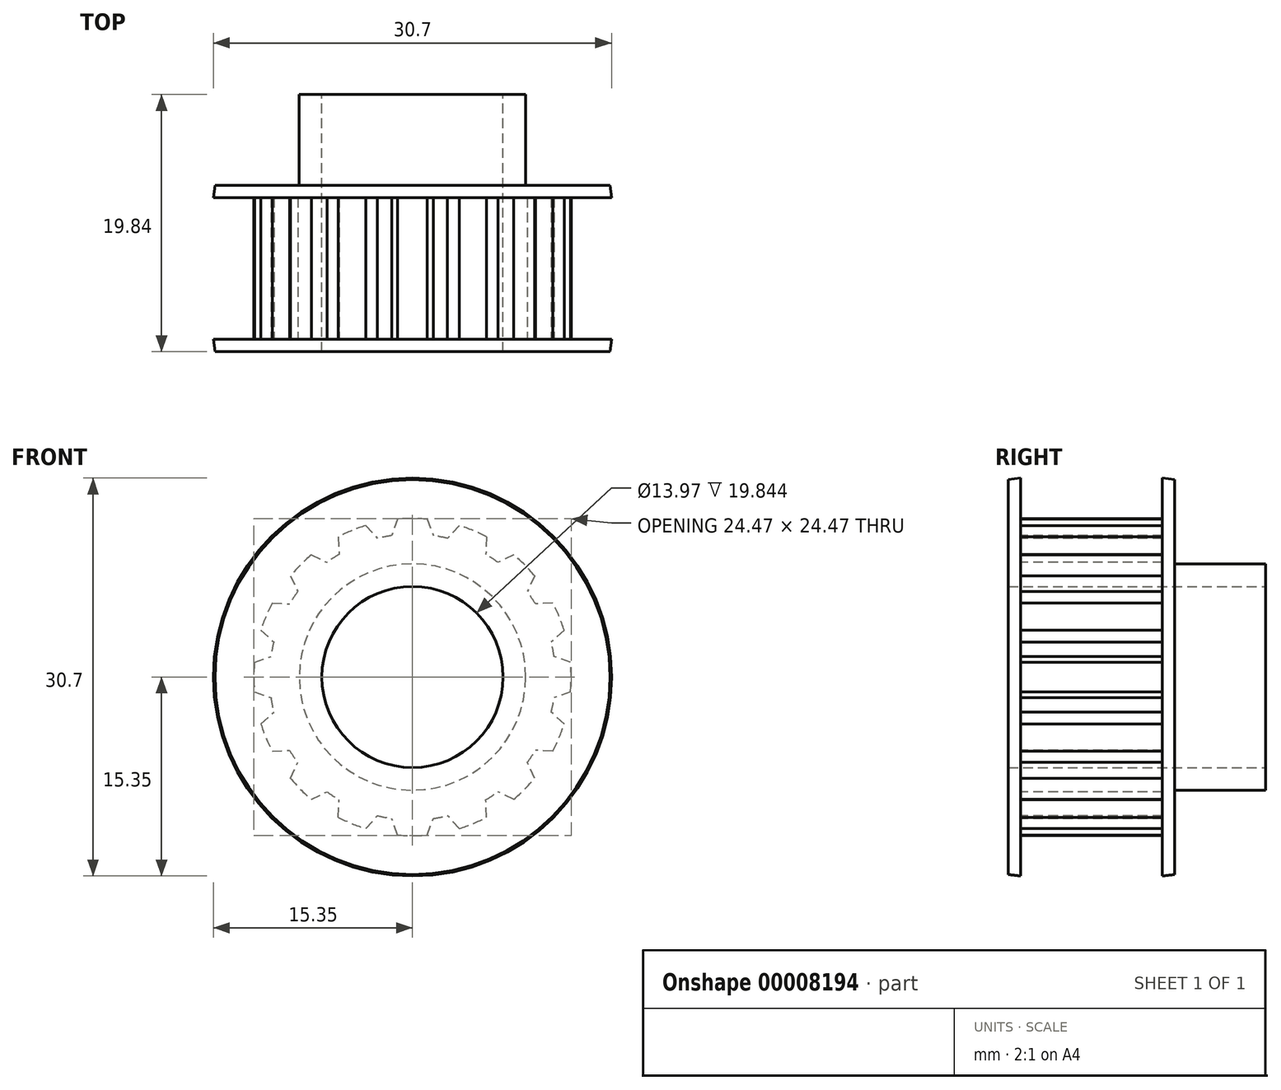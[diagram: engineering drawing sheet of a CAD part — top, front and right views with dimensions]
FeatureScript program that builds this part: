
annotation { "Feature Type Name" : "Feature", "Feature Type Description" : "" }
export const myFeature = defineFeature(function(context is Context, id is Id, definition is map)
    precondition{}
    {
        {
            var Q0;
            Q0=qCreatedBy(makeId("Front.planeOp"),FACE);
            var sketch = newSketch(context, id + "F0", { "sketchPlane" : qUnion([Q0])});
            skArc(sketch, "E0", {"start": v(1.14, 12.18) * mm, "mid": v(0, 12.23) * mm, "end": v(-1.14, 12.18) * mm});
            skArc(sketch, "E1", {"start": v(2.72, 10.7) * mm, "mid": v(2.16, 10.82) * mm, "end": v(1.6, 10.91) * mm});
            skLineSegment(sketch, "E2", {"start": v(0, 0) * mm, "end": v(0, 19.84) * mm, "construction": true});
            skLineSegment(sketch, "E3", {"start": v(-1.14, 12.18) * mm, "end": v(-1.6, 10.91) * mm});
            skLineSegment(sketch, "E4", {"start": v(1.14, 12.18) * mm, "end": v(1.6, 10.91) * mm});
            skLineSegment(sketch, "E5.1.0", {"start": v(-5.71, 10.82) * mm, "end": v(-5.65, 9.47) * mm});
            skArc(sketch, "E5.1.1", {"start": v(-3.6, 11.69) * mm, "mid": v(-4.68, 11.3) * mm, "end": v(-5.71, 10.82) * mm});
            skLineSegment(sketch, "E5.1.2", {"start": v(-3.6, 11.69) * mm, "end": v(-2.7, 10.7) * mm});
            skArc(sketch, "E5.1.3", {"start": v(-1.58, 10.92) * mm, "mid": v(-2.14, 10.82) * mm, "end": v(-2.7, 10.7) * mm});
            skLineSegment(sketch, "E5.2.0", {"start": v(-9.42, 7.8) * mm, "end": v(-8.85, 6.59) * mm});
            skArc(sketch, "E5.2.1", {"start": v(-7.8, 9.42) * mm, "mid": v(-8.65, 8.65) * mm, "end": v(-9.42, 7.8) * mm});
            skLineSegment(sketch, "E5.2.2", {"start": v(-7.8, 9.42) * mm, "end": v(-6.59, 8.85) * mm});
            skArc(sketch, "E5.2.3", {"start": v(-5.64, 9.48) * mm, "mid": v(-6.12, 9.18) * mm, "end": v(-6.59, 8.85) * mm});
            skLineSegment(sketch, "E5.3.0", {"start": v(-11.69, 3.6) * mm, "end": v(-10.7, 2.7) * mm});
            skArc(sketch, "E5.3.1", {"start": v(-10.82, 5.71) * mm, "mid": v(-11.3, 4.68) * mm, "end": v(-11.69, 3.6) * mm});
            skLineSegment(sketch, "E5.3.2", {"start": v(-10.82, 5.71) * mm, "end": v(-9.47, 5.65) * mm});
            skArc(sketch, "E5.3.3", {"start": v(-8.84, 6.6) * mm, "mid": v(-9.17, 6.14) * mm, "end": v(-9.47, 5.65) * mm});
            skLineSegment(sketch, "E5.4.0", {"start": v(-12.18, -1.14) * mm, "end": v(-10.91, -1.6) * mm});
            skArc(sketch, "E5.4.1", {"start": v(-12.18, 1.14) * mm, "mid": v(-12.23, 0) * mm, "end": v(-12.18, -1.14) * mm});
            skLineSegment(sketch, "E5.4.2", {"start": v(-12.18, 1.14) * mm, "end": v(-10.91, 1.6) * mm});
            skArc(sketch, "E5.4.3", {"start": v(-10.7, 2.72) * mm, "mid": v(-10.82, 2.16) * mm, "end": v(-10.91, 1.6) * mm});
            skLineSegment(sketch, "E5.5.0", {"start": v(-10.82, -5.71) * mm, "end": v(-9.47, -5.65) * mm});
            skArc(sketch, "E5.5.1", {"start": v(-11.69, -3.6) * mm, "mid": v(-11.3, -4.68) * mm, "end": v(-10.82, -5.71) * mm});
            skLineSegment(sketch, "E5.5.2", {"start": v(-11.69, -3.6) * mm, "end": v(-10.7, -2.7) * mm});
            skArc(sketch, "E5.5.3", {"start": v(-10.92, -1.58) * mm, "mid": v(-10.82, -2.14) * mm, "end": v(-10.7, -2.7) * mm});
            skLineSegment(sketch, "E5.6.0", {"start": v(-7.8, -9.42) * mm, "end": v(-6.59, -8.85) * mm});
            skArc(sketch, "E5.6.1", {"start": v(-9.42, -7.8) * mm, "mid": v(-8.65, -8.65) * mm, "end": v(-7.8, -9.42) * mm});
            skLineSegment(sketch, "E5.6.2", {"start": v(-9.42, -7.8) * mm, "end": v(-8.85, -6.59) * mm});
            skArc(sketch, "E5.6.3", {"start": v(-9.48, -5.64) * mm, "mid": v(-9.18, -6.12) * mm, "end": v(-8.85, -6.59) * mm});
            skLineSegment(sketch, "E5.7.0", {"start": v(-3.6, -11.69) * mm, "end": v(-2.7, -10.7) * mm});
            skArc(sketch, "E5.7.1", {"start": v(-5.71, -10.82) * mm, "mid": v(-4.68, -11.3) * mm, "end": v(-3.6, -11.69) * mm});
            skLineSegment(sketch, "E5.7.2", {"start": v(-5.71, -10.82) * mm, "end": v(-5.65, -9.47) * mm});
            skArc(sketch, "E5.7.3", {"start": v(-6.6, -8.84) * mm, "mid": v(-6.14, -9.17) * mm, "end": v(-5.65, -9.47) * mm});
            skLineSegment(sketch, "E5.8.0", {"start": v(1.14, -12.18) * mm, "end": v(1.6, -10.91) * mm});
            skArc(sketch, "E5.8.1", {"start": v(-1.14, -12.18) * mm, "mid": v(0, -12.23) * mm, "end": v(1.14, -12.18) * mm});
            skLineSegment(sketch, "E5.8.2", {"start": v(-1.14, -12.18) * mm, "end": v(-1.6, -10.91) * mm});
            skArc(sketch, "E5.8.3", {"start": v(-2.72, -10.7) * mm, "mid": v(-2.16, -10.82) * mm, "end": v(-1.6, -10.91) * mm});
            skLineSegment(sketch, "E5.9.0", {"start": v(5.71, -10.82) * mm, "end": v(5.65, -9.47) * mm});
            skArc(sketch, "E5.9.1", {"start": v(3.6, -11.69) * mm, "mid": v(4.68, -11.3) * mm, "end": v(5.71, -10.82) * mm});
            skLineSegment(sketch, "E5.9.2", {"start": v(3.6, -11.69) * mm, "end": v(2.7, -10.7) * mm});
            skArc(sketch, "E5.9.3", {"start": v(1.58, -10.92) * mm, "mid": v(2.14, -10.82) * mm, "end": v(2.7, -10.7) * mm});
            skLineSegment(sketch, "E5.10.0", {"start": v(9.42, -7.8) * mm, "end": v(8.85, -6.59) * mm});
            skArc(sketch, "E5.10.1", {"start": v(7.8, -9.42) * mm, "mid": v(8.65, -8.65) * mm, "end": v(9.42, -7.8) * mm});
            skLineSegment(sketch, "E5.10.2", {"start": v(7.8, -9.42) * mm, "end": v(6.59, -8.85) * mm});
            skArc(sketch, "E5.10.3", {"start": v(5.64, -9.48) * mm, "mid": v(6.12, -9.18) * mm, "end": v(6.59, -8.85) * mm});
            skLineSegment(sketch, "E5.11.0", {"start": v(11.69, -3.6) * mm, "end": v(10.7, -2.7) * mm});
            skArc(sketch, "E5.11.1", {"start": v(10.82, -5.71) * mm, "mid": v(11.3, -4.68) * mm, "end": v(11.69, -3.6) * mm});
            skLineSegment(sketch, "E5.11.2", {"start": v(10.82, -5.71) * mm, "end": v(9.47, -5.65) * mm});
            skArc(sketch, "E5.11.3", {"start": v(8.84, -6.6) * mm, "mid": v(9.17, -6.14) * mm, "end": v(9.47, -5.65) * mm});
            skLineSegment(sketch, "E5.12.0", {"start": v(12.18, 1.14) * mm, "end": v(10.91, 1.6) * mm});
            skArc(sketch, "E5.12.1", {"start": v(12.18, -1.14) * mm, "mid": v(12.23, 0) * mm, "end": v(12.18, 1.14) * mm});
            skLineSegment(sketch, "E5.12.2", {"start": v(12.18, -1.14) * mm, "end": v(10.91, -1.6) * mm});
            skArc(sketch, "E5.12.3", {"start": v(10.7, -2.72) * mm, "mid": v(10.82, -2.16) * mm, "end": v(10.91, -1.6) * mm});
            skLineSegment(sketch, "E5.13.0", {"start": v(10.82, 5.71) * mm, "end": v(9.47, 5.65) * mm});
            skArc(sketch, "E5.13.1", {"start": v(11.69, 3.6) * mm, "mid": v(11.3, 4.68) * mm, "end": v(10.82, 5.71) * mm});
            skLineSegment(sketch, "E5.13.2", {"start": v(11.69, 3.6) * mm, "end": v(10.7, 2.7) * mm});
            skArc(sketch, "E5.13.3", {"start": v(10.92, 1.58) * mm, "mid": v(10.82, 2.14) * mm, "end": v(10.7, 2.7) * mm});
            skLineSegment(sketch, "E5.14.0", {"start": v(7.8, 9.42) * mm, "end": v(6.59, 8.85) * mm});
            skArc(sketch, "E5.14.1", {"start": v(9.42, 7.8) * mm, "mid": v(8.65, 8.65) * mm, "end": v(7.8, 9.42) * mm});
            skLineSegment(sketch, "E5.14.2", {"start": v(9.42, 7.8) * mm, "end": v(8.85, 6.59) * mm});
            skArc(sketch, "E5.14.3", {"start": v(9.48, 5.64) * mm, "mid": v(9.18, 6.12) * mm, "end": v(8.85, 6.59) * mm});
            skLineSegment(sketch, "E5.15.0", {"start": v(3.6, 11.69) * mm, "end": v(2.7, 10.7) * mm});
            skArc(sketch, "E5.15.1", {"start": v(5.71, 10.82) * mm, "mid": v(4.68, 11.3) * mm, "end": v(3.6, 11.69) * mm});
            skLineSegment(sketch, "E5.15.2", {"start": v(5.71, 10.82) * mm, "end": v(5.65, 9.47) * mm});
            skArc(sketch, "E5.15.3", {"start": v(6.6, 8.84) * mm, "mid": v(6.14, 9.17) * mm, "end": v(5.65, 9.47) * mm});
            skSolve(sketch);
        }
        {
            var Q0;
            Q0=makeQuery(id+"F0.imprint","IMPRINT",FACE,{"disambiguationData":[TD([[makeQuery(id+"F0.imprint","IMPRINT",EDGE,{"derivedFrom":sQuery(id+"F0.wireOp",EDGE,"E0")}),1.0]])]});
            extrude(context, id + "F1", {"entities" : qUnion([Q0]), "oppositeDirection" : true, "depth" : 10.92 * mm});
        }
        {
            var Q0;
            Q0=makeQuery(id+"F1.opExtrude","CAP_FACE",FACE,{"disambiguationData":[OSD([sQuery(id+"F0.wireOp",EDGE,"E0"),sQuery(id+"F0.wireOp",EDGE,"E1"),sQuery(id+"F0.wireOp",EDGE,"E3"),sQuery(id+"F0.wireOp",EDGE,"E4"),sQuery(id+"F0.wireOp",EDGE,"E5.1.0"),sQuery(id+"F0.wireOp",EDGE,"E5.1.1"),sQuery(id+"F0.wireOp",EDGE,"E5.1.2"),sQuery(id+"F0.wireOp",EDGE,"E5.1.3"),sQuery(id+"F0.wireOp",EDGE,"E5.2.0"),sQuery(id+"F0.wireOp",EDGE,"E5.2.1"),sQuery(id+"F0.wireOp",EDGE,"E5.2.2"),sQuery(id+"F0.wireOp",EDGE,"E5.2.3"),sQuery(id+"F0.wireOp",EDGE,"E5.3.0"),sQuery(id+"F0.wireOp",EDGE,"E5.3.1"),sQuery(id+"F0.wireOp",EDGE,"E5.3.2"),sQuery(id+"F0.wireOp",EDGE,"E5.3.3"),sQuery(id+"F0.wireOp",EDGE,"E5.4.0"),sQuery(id+"F0.wireOp",EDGE,"E5.4.1"),sQuery(id+"F0.wireOp",EDGE,"E5.4.2"),sQuery(id+"F0.wireOp",EDGE,"E5.4.3"),sQuery(id+"F0.wireOp",EDGE,"E5.5.0"),sQuery(id+"F0.wireOp",EDGE,"E5.5.1"),sQuery(id+"F0.wireOp",EDGE,"E5.5.2"),sQuery(id+"F0.wireOp",EDGE,"E5.5.3"),sQuery(id+"F0.wireOp",EDGE,"E5.6.0"),sQuery(id+"F0.wireOp",EDGE,"E5.6.1"),sQuery(id+"F0.wireOp",EDGE,"E5.6.2"),sQuery(id+"F0.wireOp",EDGE,"E5.6.3"),sQuery(id+"F0.wireOp",EDGE,"E5.7.0"),sQuery(id+"F0.wireOp",EDGE,"E5.7.1"),sQuery(id+"F0.wireOp",EDGE,"E5.7.2"),sQuery(id+"F0.wireOp",EDGE,"E5.7.3"),sQuery(id+"F0.wireOp",EDGE,"E5.8.0"),sQuery(id+"F0.wireOp",EDGE,"E5.8.1"),sQuery(id+"F0.wireOp",EDGE,"E5.8.2"),sQuery(id+"F0.wireOp",EDGE,"E5.8.3"),sQuery(id+"F0.wireOp",EDGE,"E5.9.0"),sQuery(id+"F0.wireOp",EDGE,"E5.9.1"),sQuery(id+"F0.wireOp",EDGE,"E5.9.2"),sQuery(id+"F0.wireOp",EDGE,"E5.9.3"),sQuery(id+"F0.wireOp",EDGE,"E5.10.0"),sQuery(id+"F0.wireOp",EDGE,"E5.10.1"),sQuery(id+"F0.wireOp",EDGE,"E5.10.2"),sQuery(id+"F0.wireOp",EDGE,"E5.10.3"),sQuery(id+"F0.wireOp",EDGE,"E5.11.0"),sQuery(id+"F0.wireOp",EDGE,"E5.11.1"),sQuery(id+"F0.wireOp",EDGE,"E5.11.2"),sQuery(id+"F0.wireOp",EDGE,"E5.11.3"),sQuery(id+"F0.wireOp",EDGE,"E5.12.0"),sQuery(id+"F0.wireOp",EDGE,"E5.12.1"),sQuery(id+"F0.wireOp",EDGE,"E5.12.2"),sQuery(id+"F0.wireOp",EDGE,"E5.12.3"),sQuery(id+"F0.wireOp",EDGE,"E5.13.0"),sQuery(id+"F0.wireOp",EDGE,"E5.13.1"),sQuery(id+"F0.wireOp",EDGE,"E5.13.2"),sQuery(id+"F0.wireOp",EDGE,"E5.13.3"),sQuery(id+"F0.wireOp",EDGE,"E5.14.0"),sQuery(id+"F0.wireOp",EDGE,"E5.14.1"),sQuery(id+"F0.wireOp",EDGE,"E5.14.2"),sQuery(id+"F0.wireOp",EDGE,"E5.14.3"),sQuery(id+"F0.wireOp",EDGE,"E5.15.0"),sQuery(id+"F0.wireOp",EDGE,"E5.15.1"),sQuery(id+"F0.wireOp",EDGE,"E5.15.2"),sQuery(id+"F0.wireOp",EDGE,"E5.15.3")])],"isStart":true});
            var sketch = newSketch(context, id + "F2", { "sketchPlane" : qUnion([Q0])});
            skCircle(sketch, "E6", {"center": v(0, 0) * mm, "radius": 12.3 * mm});
            skSolve(sketch);
        }
        {
            var Q0;
            Q0 = qSketchRegion(id + "F2", true);
            extrude(context, id + "F3", {"entities" : qUnion([Q0]), "operationType" : NewBodyOperationType.ADD, "depth" : 0.96 * mm});
        }
        {
            var Q0;
            Q0=makeQuery(id+"F1.opExtrude","CAP_FACE",FACE,{"disambiguationData":[OSD([sQuery(id+"F0.wireOp",EDGE,"E0"),sQuery(id+"F0.wireOp",EDGE,"E1"),sQuery(id+"F0.wireOp",EDGE,"E3"),sQuery(id+"F0.wireOp",EDGE,"E4"),sQuery(id+"F0.wireOp",EDGE,"E5.1.0"),sQuery(id+"F0.wireOp",EDGE,"E5.1.1"),sQuery(id+"F0.wireOp",EDGE,"E5.1.2"),sQuery(id+"F0.wireOp",EDGE,"E5.1.3"),sQuery(id+"F0.wireOp",EDGE,"E5.2.0"),sQuery(id+"F0.wireOp",EDGE,"E5.2.1"),sQuery(id+"F0.wireOp",EDGE,"E5.2.2"),sQuery(id+"F0.wireOp",EDGE,"E5.2.3"),sQuery(id+"F0.wireOp",EDGE,"E5.3.0"),sQuery(id+"F0.wireOp",EDGE,"E5.3.1"),sQuery(id+"F0.wireOp",EDGE,"E5.3.2"),sQuery(id+"F0.wireOp",EDGE,"E5.3.3"),sQuery(id+"F0.wireOp",EDGE,"E5.4.0"),sQuery(id+"F0.wireOp",EDGE,"E5.4.1"),sQuery(id+"F0.wireOp",EDGE,"E5.4.2"),sQuery(id+"F0.wireOp",EDGE,"E5.4.3"),sQuery(id+"F0.wireOp",EDGE,"E5.5.0"),sQuery(id+"F0.wireOp",EDGE,"E5.5.1"),sQuery(id+"F0.wireOp",EDGE,"E5.5.2"),sQuery(id+"F0.wireOp",EDGE,"E5.5.3"),sQuery(id+"F0.wireOp",EDGE,"E5.6.0"),sQuery(id+"F0.wireOp",EDGE,"E5.6.1"),sQuery(id+"F0.wireOp",EDGE,"E5.6.2"),sQuery(id+"F0.wireOp",EDGE,"E5.6.3"),sQuery(id+"F0.wireOp",EDGE,"E5.7.0"),sQuery(id+"F0.wireOp",EDGE,"E5.7.1"),sQuery(id+"F0.wireOp",EDGE,"E5.7.2"),sQuery(id+"F0.wireOp",EDGE,"E5.7.3"),sQuery(id+"F0.wireOp",EDGE,"E5.8.0"),sQuery(id+"F0.wireOp",EDGE,"E5.8.1"),sQuery(id+"F0.wireOp",EDGE,"E5.8.2"),sQuery(id+"F0.wireOp",EDGE,"E5.8.3"),sQuery(id+"F0.wireOp",EDGE,"E5.9.0"),sQuery(id+"F0.wireOp",EDGE,"E5.9.1"),sQuery(id+"F0.wireOp",EDGE,"E5.9.2"),sQuery(id+"F0.wireOp",EDGE,"E5.9.3"),sQuery(id+"F0.wireOp",EDGE,"E5.10.0"),sQuery(id+"F0.wireOp",EDGE,"E5.10.1"),sQuery(id+"F0.wireOp",EDGE,"E5.10.2"),sQuery(id+"F0.wireOp",EDGE,"E5.10.3"),sQuery(id+"F0.wireOp",EDGE,"E5.11.0"),sQuery(id+"F0.wireOp",EDGE,"E5.11.1"),sQuery(id+"F0.wireOp",EDGE,"E5.11.2"),sQuery(id+"F0.wireOp",EDGE,"E5.11.3"),sQuery(id+"F0.wireOp",EDGE,"E5.12.0"),sQuery(id+"F0.wireOp",EDGE,"E5.12.1"),sQuery(id+"F0.wireOp",EDGE,"E5.12.2"),sQuery(id+"F0.wireOp",EDGE,"E5.12.3"),sQuery(id+"F0.wireOp",EDGE,"E5.13.0"),sQuery(id+"F0.wireOp",EDGE,"E5.13.1"),sQuery(id+"F0.wireOp",EDGE,"E5.13.2"),sQuery(id+"F0.wireOp",EDGE,"E5.13.3"),sQuery(id+"F0.wireOp",EDGE,"E5.14.0"),sQuery(id+"F0.wireOp",EDGE,"E5.14.1"),sQuery(id+"F0.wireOp",EDGE,"E5.14.2"),sQuery(id+"F0.wireOp",EDGE,"E5.14.3"),sQuery(id+"F0.wireOp",EDGE,"E5.15.0"),sQuery(id+"F0.wireOp",EDGE,"E5.15.1"),sQuery(id+"F0.wireOp",EDGE,"E5.15.2"),sQuery(id+"F0.wireOp",EDGE,"E5.15.3")])],"isStart":false});
            var sketch = newSketch(context, id + "F4", { "sketchPlane" : qUnion([Q0])});
            skCircle(sketch, "E7", {"center": v(0, 0) * mm, "radius": 12.3 * mm});
            skSolve(sketch);
        }
        {
            var Q0;
            Q0 = qSketchRegion(id + "F4", true);
            extrude(context, id + "F5", {"entities" : qUnion([Q0]), "operationType" : NewBodyOperationType.ADD, "depth" : 0.96 * mm});
        }
        {
            var Q0;
            Q0=makeQuery(id+"F5.opExtrude","CAP_FACE",FACE,{"disambiguationData":[OSD([sQuery(id+"F4.wireOp",EDGE,"E7")])],"isStart":false});
            var sketch = newSketch(context, id + "F6", { "sketchPlane" : qUnion([Q0])});
            skCircle(sketch, "E8", {"center": v(0, 0) * mm, "radius": 8.73 * mm});
            skSolve(sketch);
        }
        {
            var Q0;
            Q0 = qSketchRegion(id + "F6", true);
            extrude(context, id + "F7", {"entities" : qUnion([Q0]), "operationType" : NewBodyOperationType.ADD, "depth" : 7 * mm});
        }
        {
            var Q0;
            Q0=makeQuery(id+"F7.opExtrude","CAP_FACE",FACE,{"disambiguationData":[OSD([sQuery(id+"F6.wireOp",EDGE,"E8")])],"isStart":false});
            var sketch = newSketch(context, id + "F8", { "sketchPlane" : qUnion([Q0])});
            skCircle(sketch, "E9", {"center": v(0, 0) * mm, "radius": 6.99 * mm});
            skSolve(sketch);
        }
        {
            var Q0;
            Q0 = qSketchRegion(id + "F8", true);
            var Q1;
            Q1=makeQuery(id+"F3.opExtrude","CAP_FACE",FACE,{"disambiguationData":[OSD([sQuery(id+"F2.wireOp",EDGE,"E6")])],"isStart":false});
            extrude(context, id + "F9", {"entities" : qUnion([Q0]), "operationType" : NewBodyOperationType.REMOVE, "endBound" : BoundingType.UP_TO_SURFACE, "oppositeDirection" : true, "endBoundEntityFace" : qUnion([Q1]), "depth" : 25.4 * mm});
        }
        {
            var Q0;
            Q0=qCreatedBy(makeId("Right.planeOp"),FACE);
            var sketch = newSketch(context, id + "F10", { "sketchPlane" : qUnion([Q0])});
            skLineSegment(sketch, "E10", {"start": v(-0.96, 12.3) * mm, "end": v(0, 12.3) * mm});
            skLineSegment(sketch, "E11", {"start": v(0, 12.3) * mm, "end": v(0, 15.35) * mm});
            skLineSegment(sketch, "E12", {"start": v(0, 15.35) * mm, "end": v(-0.96, 15.23) * mm});
            skLineSegment(sketch, "E13", {"start": v(-0.96, 15.23) * mm, "end": v(-0.96, 12.3) * mm});
            skLineSegment(sketch, "E14", {"start": v(-5.59, 12.3) * mm, "end": v(14.67, 12.3) * mm, "construction": true});
            skLineSegment(sketch, "E15", {"start": v(11.88, 12.3) * mm, "end": v(10.92, 12.3) * mm});
            skLineSegment(sketch, "E16", {"start": v(10.92, 12.3) * mm, "end": v(10.92, 15.35) * mm});
            skLineSegment(sketch, "E17", {"start": v(10.92, 15.35) * mm, "end": v(11.88, 15.23) * mm});
            skLineSegment(sketch, "E18", {"start": v(11.88, 15.23) * mm, "end": v(11.88, 12.3) * mm});
            skLineSegment(sketch, "E19", {"start": v(0, 0) * mm, "end": v(23.02, 0) * mm, "construction": true});
            skSolve(sketch);
        }
        {
            var Q0;
            Q0 = qSketchRegion(id + "F10", true);
            var Q1;
            Q1=sQuery(id+"F10.wireOp",EDGE,"E19");
            revolve(context, id + "F11", {"operationType" : NewBodyOperationType.ADD, "entities" : qUnion([Q0]), "axis" : qUnion([Q1]), "revolveType" : RevolveType.FULL});
        }
    });
